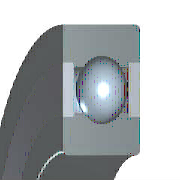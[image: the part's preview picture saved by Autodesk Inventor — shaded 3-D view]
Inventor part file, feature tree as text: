
AUTODESK INVENTOR PART (.ipt)
format: ipt  version: 2025.2 (Build 292293000, 293)  size: 348,160 bytes
history: native  units: mm (DEFAULTED — no unit token found)
features: other x1, pattern_circular x1
ambient origin geometry x8: Origin, YZ Plane, XZ Plane, XY Plane, X Axis, Y Axis, Z Axis, Center Point
bodies: Solid1 (feature_tree), Body (feature_tree)
feature tree (2):
  other  "Ball"
  pattern_circular  "Balls"  [2 undecoded]
note: 2 required parameter values undecoded (feature->parameter linkage not recoverable at this tier; creation-order binding heuristic only, values carry confidence <= 0.55)
